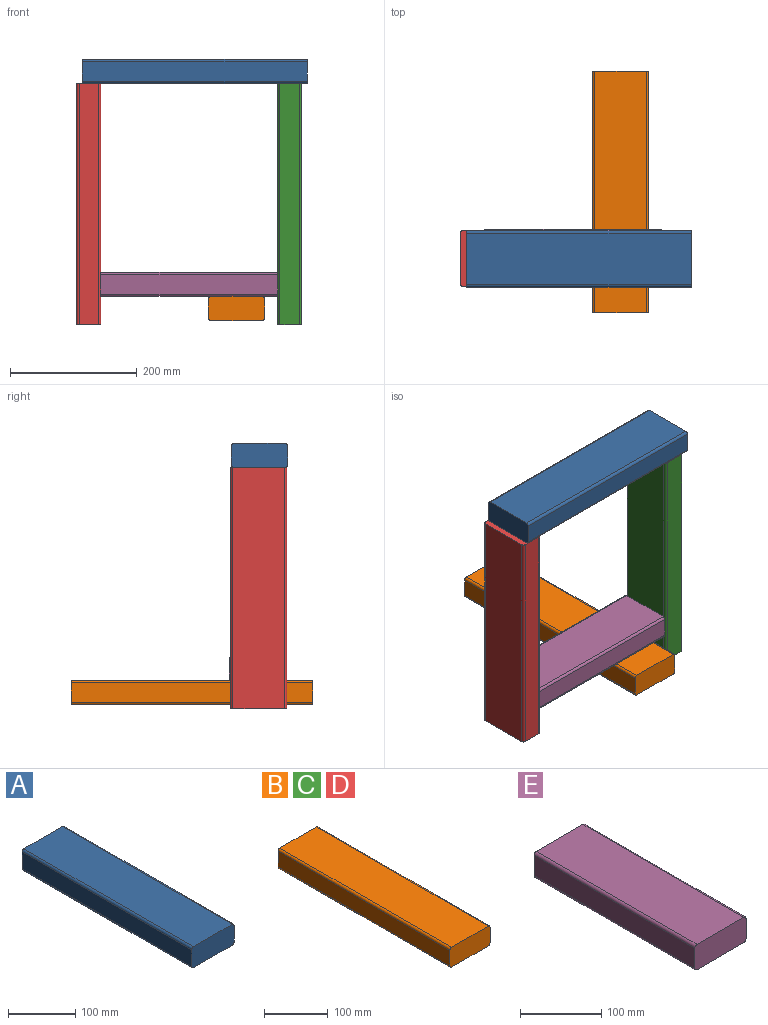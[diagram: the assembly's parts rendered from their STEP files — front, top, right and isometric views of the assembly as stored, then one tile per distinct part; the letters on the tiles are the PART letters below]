
ASSEMBLY  parts=5 mates=5
PART A: 10 faces, bbox 88.9x355.6x38.1 mm
  f0: plane 355.6x81.28mm, normal (0,0,1), area 28903.2mm2, adj f4,f5,f6,f9
  f1: plane 355.6x30.48mm, normal (-1,0,0), area 10838.7mm2, adj f4,f5,f6,f7
  f2: plane 355.6x81.28mm, normal (0,0,-1), area 28903.2mm2, adj f4,f5,f7,f8
  f3: plane 355.6x30.48mm, normal (1,0,0), area 10838.7mm2, adj f4,f5,f8,f9
  f4: plane 88.9x38.1mm, normal (0,1,0), area 3374.6mm2, adj f0,f1,f2,f3,f6,f7,f8,f9
  f5: plane 88.9x38.1mm, normal (0,-1,0), area 3374.6mm2, adj f0,f1,f2,f3,f6,f7,f8,f9
  f6: cylinder r=3.81mm len=355.6mm, axis (0,1,0), area 2128.2mm2, adj f0,f1,f4,f5
  f7: cylinder r=3.81mm len=355.6mm, axis (0,-1,0), area 2128.2mm2, adj f1,f2,f4,f5
  f8: cylinder r=3.81mm len=355.6mm, axis (0,1,0), area 2128.2mm2, adj f2,f3,f4,f5
  f9: cylinder r=3.81mm len=355.6mm, axis (0,-1,0), area 2128.2mm2, adj f0,f3,f4,f5
PART B: 10 faces, bbox 88.9x381x38.1 mm
  f0: plane 381x81.28mm, normal (0,0,1), area 30967.7mm2, adj f4,f5,f6,f9
  f1: plane 381x30.48mm, normal (-1,0,0), area 11612.9mm2, adj f4,f5,f6,f7
  f2: plane 381x81.28mm, normal (0,0,-1), area 30967.7mm2, adj f4,f5,f7,f8
  f3: plane 381x30.48mm, normal (1,0,0), area 11612.9mm2, adj f4,f5,f8,f9
  f4: plane 88.9x38.1mm, normal (0,1,0), area 3374.6mm2, adj f0,f1,f2,f3,f6,f7,f8,f9
  f5: plane 88.9x38.1mm, normal (0,-1,0), area 3374.6mm2, adj f0,f1,f2,f3,f6,f7,f8,f9
  f6: cylinder r=3.81mm len=381mm, axis (0,1,0), area 2280.2mm2, adj f0,f1,f4,f5
  f7: cylinder r=3.81mm len=381mm, axis (0,-1,0), area 2280.2mm2, adj f1,f2,f4,f5
  f8: cylinder r=3.81mm len=381mm, axis (0,1,0), area 2280.2mm2, adj f2,f3,f4,f5
  f9: cylinder r=3.81mm len=381mm, axis (0,-1,0), area 2280.2mm2, adj f0,f3,f4,f5
PART C: same geometry as B
PART D: same geometry as B
PART E: 10 faces, bbox 88.9x279.4x38.1 mm
  f0: plane 279.4x81.28mm, normal (0,0,1), area 22709.6mm2, adj f4,f5,f6,f9
  f1: plane 279.4x30.48mm, normal (-1,0,0), area 8516.1mm2, adj f4,f5,f6,f7
  f2: plane 279.4x81.28mm, normal (0,0,-1), area 22709.6mm2, adj f4,f5,f7,f8
  f3: plane 279.4x30.48mm, normal (1,0,0), area 8516.1mm2, adj f4,f5,f8,f9
  f4: plane 88.9x38.1mm, normal (0,1,0), area 3374.6mm2, adj f0,f1,f2,f3,f6,f7,f8,f9
  f5: plane 88.9x38.1mm, normal (0,-1,0), area 3374.6mm2, adj f0,f1,f2,f3,f6,f7,f8,f9
  f6: cylinder r=3.81mm len=279.4mm, axis (0,1,0), area 1672.1mm2, adj f0,f1,f4,f5
  f7: cylinder r=3.81mm len=279.4mm, axis (0,-1,0), area 1672.1mm2, adj f1,f2,f4,f5
  f8: cylinder r=3.81mm len=279.4mm, axis (0,1,0), area 1672.1mm2, adj f2,f3,f4,f5
  f9: cylinder r=3.81mm len=279.4mm, axis (0,-1,0), area 1672.1mm2, adj f0,f3,f4,f5
PLACE A rot(axis=(0,0,-1),90deg) t=(-99.98,-27.78,2.19)mm
PLACE B t=(99.21,-156.15,-372.48)mm
PLACE C rot(axis=(-0.58,0.58,-0.58),120deg) t=(246.55,-26.48,-35.91)mm
PLACE D rot(axis=(-0.58,0.58,-0.58),120deg) t=(-70.95,-26.48,-35.91)mm
PLACE E rot(axis=(0,0,1),90deg) t=(208.45,-113.57,-334.38)mm
MATE planar B.f0 <-> E.f2  axis (0,0,1) through (143.66,34.35,-372.48)mm
MATE planar E.f4 <-> D.f0  axis (-1,0,0) through (-70.95,-69.12,-353.43)mm
MATE planar C.f5 <-> A.f2  axis (0,0,1) through (246.55,-70.93,-35.91)mm
MATE planar A.f2 <-> D.f5  axis (0,0,-1) through (-99.98,-72.23,-35.91)mm
MATE planar E.f5 <-> C.f2  axis (1,0,0) through (208.45,-69.12,-372.48)mm
